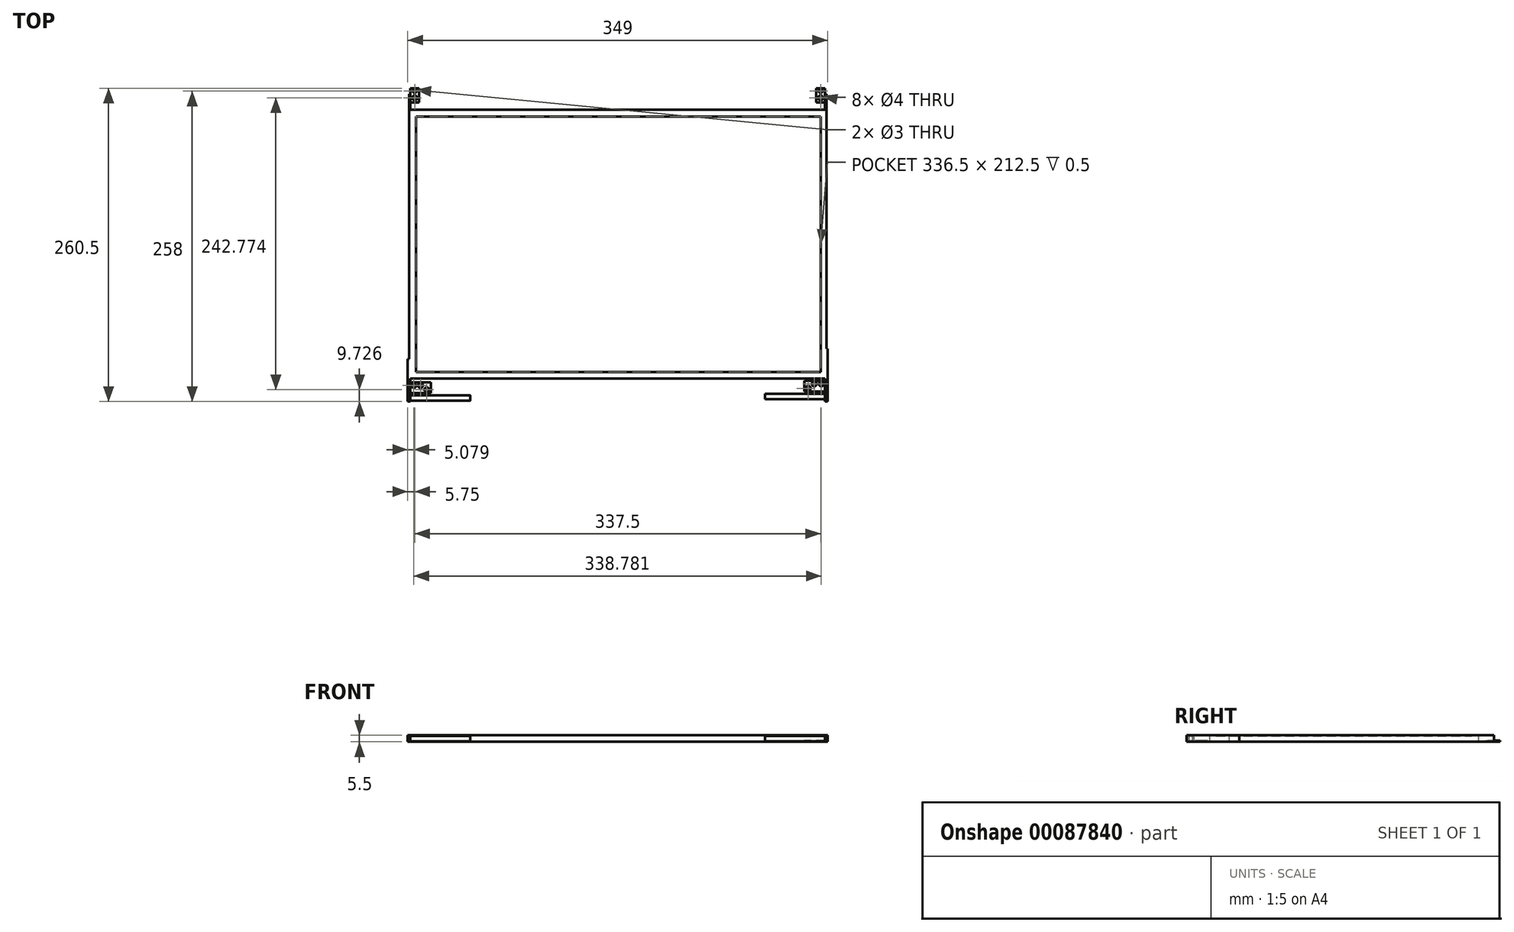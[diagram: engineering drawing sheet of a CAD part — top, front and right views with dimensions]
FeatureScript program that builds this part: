
annotation { "Feature Type Name" : "Feature", "Feature Type Description" : "" }
export const myFeature = defineFeature(function(context is Context, id is Id, definition is map)
    precondition{}
    {
        {
            var Q0;
            Q0=qCreatedBy(makeId("Top.planeOp"),FACE);
            var sketch = newSketch(context, id + "F0", { "sketchPlane" : qUnion([Q0])});
            skLineSegment(sketch, "E0.bottom", {"start": v(172.5, -111.75) * mm, "end": v(-172.5, -111.75) * mm});
            skLineSegment(sketch, "E0.top", {"start": v(172.5, 111.75) * mm, "end": v(-172.5, 111.75) * mm});
            skLineSegment(sketch, "E0.left", {"start": v(172.5, -111.75) * mm, "end": v(172.5, 111.75) * mm});
            skLineSegment(sketch, "E0.right", {"start": v(-172.5, -111.75) * mm, "end": v(-172.5, 111.75) * mm});
            skPoint(sketch, "E0.middle", {"position": v(0, 0) * mm});
            skSolve(sketch);
        }
        {
            var Q0;
            Q0 = qSketchRegion(id + "F0", true);
            extrude(context, id + "F1", {"entities" : qUnion([Q0]), "depth" : 5.5 * mm, "symmetric" : true});
        }
        {
            var Q0;
            Q0=makeQuery(id+"F1.opExtrude","CAP_FACE",FACE,{"disambiguationData":[OSD([sQuery(id+"F0.wireOp",EDGE,"E0.bottom"),sQuery(id+"F0.wireOp",EDGE,"E0.top"),sQuery(id+"F0.wireOp",EDGE,"E0.left"),sQuery(id+"F0.wireOp",EDGE,"E0.right")])],"isStart":false});
            var sketch = newSketch(context, id + "F2", { "sketchPlane" : qUnion([Q0])});
            skLineSegment(sketch, "E1.bottom", {"start": v(169, -106.25) * mm, "end": v(-167.5, -106.25) * mm});
            skLineSegment(sketch, "E1.top", {"start": v(169, 106.25) * mm, "end": v(-167.5, 106.25) * mm});
            skLineSegment(sketch, "E1.left", {"start": v(169, -106.25) * mm, "end": v(169, 106.25) * mm});
            skLineSegment(sketch, "E1.right", {"start": v(-167.5, -106.25) * mm, "end": v(-167.5, 106.25) * mm});
            skPoint(sketch, "E1.middle", {"position": v(0, 0) * mm});
            skSolve(sketch);
        }
        {
            var Q0;
            Q0 = qSketchRegion(id + "F2", true);
            var Q1;
            Q1 = qConstructionFilter(qBodyType(qCreatedBy(id + "F2" ,EDGE), BodyType.WIRE), ConstructionObject.NO);
            extrude(context, id + "F3", {"entities" : qUnion([Q0]), "operationType" : NewBodyOperationType.REMOVE, "surfaceEntities" : qUnion([Q1]), "oppositeDirection" : true, "depth" : 0.5 * mm});
        }
        {
            var Q0;
            Q0=makeQuery(id+"F1.opExtrude","SWEPT_FACE",FACE,{"disambiguationData":[OSD([sQuery(id+"F0.wireOp",EDGE,"E0.right")])]});
            var sketch = newSketch(context, id + "F4", { "sketchPlane" : qUnion([Q0])});
            skLineSegment(sketch, "E2", {"start": v(-124.75, 2.75) * mm, "end": v(-111.75, 2.75) * mm});
            skLineSegment(sketch, "E3", {"start": v(-111.75, 2.75) * mm, "end": v(111.75, 2.75) * mm});
            skLineSegment(sketch, "E4", {"start": v(111.75, 2.75) * mm, "end": v(130.75, 2.75) * mm});
            skLineSegment(sketch, "E5", {"start": v(130.75, 2.75) * mm, "end": v(130.75, -2.75) * mm});
            skLineSegment(sketch, "E6", {"start": v(130.75, -2.75) * mm, "end": v(111.75, -2.75) * mm});
            skLineSegment(sketch, "E7", {"start": v(111.75, -2.75) * mm, "end": v(-111.75, -2.75) * mm});
            skLineSegment(sketch, "E8", {"start": v(-111.75, -2.75) * mm, "end": v(-124.75, -2.75) * mm});
            skLineSegment(sketch, "E9", {"start": v(-124.75, -2.75) * mm, "end": v(-124.75, 2.75) * mm});
            skSolve(sketch);
        }
        {
            var Q0;
            Q0 = qSketchRegion(id + "F4", true);
            extrude(context, id + "F5", {"entities" : qUnion([Q0]), "operationType" : NewBodyOperationType.ADD, "depth" : 1 * mm});
        }
        {
            var Q0;
            Q0=makeQuery(id+"F1.opExtrude","SWEPT_FACE",FACE,{"disambiguationData":[OSD([sQuery(id+"F0.wireOp",EDGE,"E0.left")])]});
            var sketch = newSketch(context, id + "F6", { "sketchPlane" : qUnion([Q0])});
            skLineSegment(sketch, "E10", {"start": v(111.75, 2.75) * mm, "end": v(124.75, 2.75) * mm});
            skLineSegment(sketch, "E11", {"start": v(124.75, 2.75) * mm, "end": v(124.75, -2.75) * mm});
            skLineSegment(sketch, "E12", {"start": v(124.75, -2.75) * mm, "end": v(111.75, -2.75) * mm});
            skLineSegment(sketch, "E13", {"start": v(111.75, -2.75) * mm, "end": v(-111.75, -2.75) * mm});
            skLineSegment(sketch, "E14", {"start": v(-111.75, -2.75) * mm, "end": v(-130.75, -2.75) * mm});
            skLineSegment(sketch, "E15", {"start": v(-130.75, -2.75) * mm, "end": v(-130.75, 2.75) * mm});
            skLineSegment(sketch, "E16", {"start": v(-130.75, 2.75) * mm, "end": v(-111.75, 2.75) * mm});
            skLineSegment(sketch, "E17", {"start": v(-111.75, 2.75) * mm, "end": v(111.75, 2.75) * mm});
            skSolve(sketch);
        }
        {
            var Q0;
            Q0 = qSketchRegion(id + "F6", true);
            extrude(context, id + "F7", {"entities" : qUnion([Q0]), "operationType" : NewBodyOperationType.ADD, "depth" : 1 * mm});
        }
        {
            var Q0;
            Q0=makeQuery(id+"F7.boolean.opBoolean","MERGE",FACE,{"derivedFrom":[makeQuery(id+"F5.boolean.opBoolean","MERGE",FACE,{"derivedFrom":[makeQuery(id+"F1.opExtrude","CAP_FACE",FACE,{"disambiguationData":[OSD([sQuery(id+"F0.wireOp",EDGE,"E0.bottom"),sQuery(id+"F0.wireOp",EDGE,"E0.top"),sQuery(id+"F0.wireOp",EDGE,"E0.left"),sQuery(id+"F0.wireOp",EDGE,"E0.right")])],"isStart":true}),makeQuery(id+"F5.opExtrude","SWEPT_FACE",FACE,{"disambiguationData":[OSD([sQuery(id+"F4.wireOp",EDGE,"E6"),sQuery(id+"F4.wireOp",EDGE,"E7"),sQuery(id+"F4.wireOp",EDGE,"E8")])]})]}),makeQuery(id+"F7.opExtrude","SWEPT_FACE",FACE,{"disambiguationData":[OSD([sQuery(id+"F6.wireOp",EDGE,"E12"),sQuery(id+"F6.wireOp",EDGE,"E13"),sQuery(id+"F6.wireOp",EDGE,"E14")])]})]});
            var sketch = newSketch(context, id + "F8", { "sketchPlane" : qUnion([Q0])});
            skLineSegment(sketch, "E18", {"start": v(-172.5, -124.75) * mm, "end": v(-172.5, -117.75) * mm});
            skLineSegment(sketch, "E19", {"start": v(-172.5, -117.75) * mm, "end": v(-165, -117.75) * mm});
            skLineSegment(sketch, "E20", {"start": v(-165, -117.75) * mm, "end": v(-165, -129.75) * mm});
            skLineSegment(sketch, "E21", {"start": v(-165, -129.75) * mm, "end": v(-172.5, -129.75) * mm});
            skLineSegment(sketch, "E22", {"start": v(-172.5, -129.75) * mm, "end": v(-172.5, -124.75) * mm});
            skCircle(sketch, "E23", {"center": v(-168.75, -121.75) * mm, "radius": 2 * mm});
            skCircle(sketch, "E24", {"center": v(-168.75, -127.25) * mm, "radius": 1.5 * mm});
            skSolve(sketch);
        }
        {
            var Q0;
            Q0=makeQuery(id+"F8.imprint","IMPRINT",FACE,{"disambiguationData":[TD([[makeQuery(id+"F8.imprint","IMPRINT",EDGE,{"derivedFrom":sQuery(id+"F8.wireOp",EDGE,"E18")}),1.0]])]});
            extrude(context, id + "F9", {"entities" : qUnion([Q0]), "operationType" : NewBodyOperationType.ADD, "oppositeDirection" : true, "depth" : 1 * mm});
        }
        {
            var Q0;
            Q0=makeQuery(id+"F9.boolean.opBoolean","MERGE",FACE,{"derivedFrom":[makeQuery(id+"F7.boolean.opBoolean","MERGE",FACE,{"derivedFrom":[makeQuery(id+"F5.boolean.opBoolean","MERGE",FACE,{"derivedFrom":[makeQuery(id+"F1.opExtrude","CAP_FACE",FACE,{"disambiguationData":[OSD([sQuery(id+"F0.wireOp",EDGE,"E0.bottom"),sQuery(id+"F0.wireOp",EDGE,"E0.top"),sQuery(id+"F0.wireOp",EDGE,"E0.left"),sQuery(id+"F0.wireOp",EDGE,"E0.right")])],"isStart":true}),makeQuery(id+"F5.opExtrude","SWEPT_FACE",FACE,{"disambiguationData":[OSD([sQuery(id+"F4.wireOp",EDGE,"E6"),sQuery(id+"F4.wireOp",EDGE,"E7"),sQuery(id+"F4.wireOp",EDGE,"E8")])]})]}),makeQuery(id+"F7.opExtrude","SWEPT_FACE",FACE,{"disambiguationData":[OSD([sQuery(id+"F6.wireOp",EDGE,"E12"),sQuery(id+"F6.wireOp",EDGE,"E13"),sQuery(id+"F6.wireOp",EDGE,"E14")])]})]}),makeQuery(id+"F9.opExtrude","CAP_FACE",FACE,{"disambiguationData":[OSD([sQuery(id+"F8.wireOp",EDGE,"E18"),sQuery(id+"F8.wireOp",EDGE,"E19"),sQuery(id+"F8.wireOp",EDGE,"E20"),sQuery(id+"F8.wireOp",EDGE,"E21"),sQuery(id+"F8.wireOp",EDGE,"E22"),sQuery(id+"F8.wireOp",EDGE,"E23"),sQuery(id+"F8.wireOp",EDGE,"E24")])],"isStart":true})]});
            var sketch = newSketch(context, id + "F10", { "sketchPlane" : qUnion([Q0])});
            skLineSegment(sketch, "E25", {"start": v(165, -129.75) * mm, "end": v(165, -117.75) * mm});
            skLineSegment(sketch, "E26", {"start": v(165, -117.75) * mm, "end": v(172.5, -117.75) * mm});
            skLineSegment(sketch, "E27", {"start": v(172.5, -117.75) * mm, "end": v(172.5, -129.75) * mm});
            skLineSegment(sketch, "E28", {"start": v(172.5, -129.75) * mm, "end": v(165, -129.75) * mm});
            skCircle(sketch, "E29", {"center": v(168.75, -121.75) * mm, "radius": 2 * mm});
            skCircle(sketch, "E30", {"center": v(168.75, -127.25) * mm, "radius": 1.5 * mm});
            skPoint(sketch, "E31", {"position": v(172.5, -124.75) * mm});
            skSolve(sketch);
        }
        {
            var Q0;
            Q0=makeQuery(id+"F10.imprint","IMPRINT",FACE,{"disambiguationData":[TD([[makeQuery(id+"F10.imprint","IMPRINT",EDGE,{"derivedFrom":sQuery(id+"F10.wireOp",EDGE,"E25")}),-1.0]])]});
            extrude(context, id + "F11", {"entities" : qUnion([Q0]), "operationType" : NewBodyOperationType.ADD, "oppositeDirection" : true, "depth" : 1 * mm});
        }
        {
            var Q0;
            Q0=makeQuery(id+"F5.opExtrude","CAP_FACE",FACE,{"disambiguationData":[OSD([sQuery(id+"F4.wireOp",EDGE,"E2"),sQuery(id+"F4.wireOp",EDGE,"E3"),sQuery(id+"F4.wireOp",EDGE,"E4"),sQuery(id+"F4.wireOp",EDGE,"E5"),sQuery(id+"F4.wireOp",EDGE,"E6"),sQuery(id+"F4.wireOp",EDGE,"E7"),sQuery(id+"F4.wireOp",EDGE,"E8"),sQuery(id+"F4.wireOp",EDGE,"E9")])],"isStart":false});
            var sketch = newSketch(context, id + "F12", { "sketchPlane" : qUnion([Q0])});
            skLineSegment(sketch, "E32.bottom", {"start": v(130.75, 2.75) * mm, "end": v(95.48, 2.75) * mm});
            skLineSegment(sketch, "E32.top", {"start": v(130.75, -2.75) * mm, "end": v(95.48, -2.75) * mm});
            skLineSegment(sketch, "E32.left", {"start": v(130.75, 2.75) * mm, "end": v(130.75, -2.75) * mm});
            skLineSegment(sketch, "E32.right", {"start": v(95.48, 2.75) * mm, "end": v(95.48, -2.75) * mm});
            skSolve(sketch);
        }
        {
            var Q0;
            Q0=makeQuery(id+"F12.imprint","IMPRINT",FACE,{"disambiguationData":[TD([[makeQuery(id+"F12.imprint","IMPRINT",EDGE,{"derivedFrom":sQuery(id+"F12.wireOp",EDGE,"E32.bottom")}),-1.0]])]});
            extrude(context, id + "F13", {"entities" : qUnion([Q0]), "operationType" : NewBodyOperationType.ADD, "depth" : 1 * mm});
        }
        {
            var Q0;
            Q0=makeQuery(id+"F13.boolean.opBoolean","MERGE",FACE,{"derivedFrom":[makeQuery(id+"F11.boolean.opBoolean","MERGE",FACE,{"derivedFrom":[makeQuery(id+"F9.boolean.opBoolean","MERGE",FACE,{"derivedFrom":[makeQuery(id+"F7.boolean.opBoolean","MERGE",FACE,{"derivedFrom":[makeQuery(id+"F5.boolean.opBoolean","MERGE",FACE,{"derivedFrom":[makeQuery(id+"F1.opExtrude","CAP_FACE",FACE,{"disambiguationData":[OSD([sQuery(id+"F0.wireOp",EDGE,"E0.bottom"),sQuery(id+"F0.wireOp",EDGE,"E0.top"),sQuery(id+"F0.wireOp",EDGE,"E0.left"),sQuery(id+"F0.wireOp",EDGE,"E0.right")])],"isStart":true}),makeQuery(id+"F5.opExtrude","SWEPT_FACE",FACE,{"disambiguationData":[OSD([sQuery(id+"F4.wireOp",EDGE,"E6"),sQuery(id+"F4.wireOp",EDGE,"E7"),sQuery(id+"F4.wireOp",EDGE,"E8")])]})]}),makeQuery(id+"F7.opExtrude","SWEPT_FACE",FACE,{"disambiguationData":[OSD([sQuery(id+"F6.wireOp",EDGE,"E12"),sQuery(id+"F6.wireOp",EDGE,"E13"),sQuery(id+"F6.wireOp",EDGE,"E14")])]})]}),makeQuery(id+"F9.opExtrude","CAP_FACE",FACE,{"disambiguationData":[OSD([sQuery(id+"F8.wireOp",EDGE,"E18"),sQuery(id+"F8.wireOp",EDGE,"E19"),sQuery(id+"F8.wireOp",EDGE,"E20"),sQuery(id+"F8.wireOp",EDGE,"E21"),sQuery(id+"F8.wireOp",EDGE,"E22"),sQuery(id+"F8.wireOp",EDGE,"E23"),sQuery(id+"F8.wireOp",EDGE,"E24")])],"isStart":true})]}),makeQuery(id+"F11.opExtrude","CAP_FACE",FACE,{"disambiguationData":[OSD([sQuery(id+"F10.wireOp",EDGE,"E25"),sQuery(id+"F10.wireOp",EDGE,"E26"),sQuery(id+"F10.wireOp",EDGE,"E27"),sQuery(id+"F10.wireOp",EDGE,"E28"),sQuery(id+"F10.wireOp",EDGE,"E29"),sQuery(id+"F10.wireOp",EDGE,"E30")])],"isStart":true})]}),makeQuery(id+"F13.opExtrude","SWEPT_FACE",FACE,{"disambiguationData":[OSD([sQuery(id+"F12.wireOp",EDGE,"E32.top")])]})]});
            var sketch = newSketch(context, id + "F14", { "sketchPlane" : qUnion([Q0])});
            skLineSegment(sketch, "E33.bottom", {"start": v(-172.5, 123.78) * mm, "end": v(-155.28, 123.78) * mm});
            skLineSegment(sketch, "E33.top", {"start": v(-172.5, 114.86) * mm, "end": v(-155.28, 114.86) * mm});
            skLineSegment(sketch, "E33.left", {"start": v(-172.5, 123.78) * mm, "end": v(-172.5, 114.86) * mm});
            skLineSegment(sketch, "E33.right", {"start": v(-155.28, 123.78) * mm, "end": v(-155.28, 114.86) * mm});
            skCircle(sketch, "E34", {"center": v(-169.42, 117.54) * mm, "radius": 2 * mm});
            skCircle(sketch, "E35", {"center": v(-163.89, 117.54) * mm, "radius": 2 * mm});
            skCircle(sketch, "E36", {"center": v(-158.69, 121.02) * mm, "radius": 2 * mm});
            skSolve(sketch);
        }
        {
            var Q0;
            Q0=makeQuery(id+"F14.imprint","IMPRINT",FACE,{"disambiguationData":[TD([[makeQuery(id+"F14.imprint","IMPRINT",EDGE,{"derivedFrom":sQuery(id+"F14.wireOp",EDGE,"E33.bottom")}),-1.0]])]});
            extrude(context, id + "F15", {"entities" : qUnion([Q0]), "operationType" : NewBodyOperationType.ADD, "oppositeDirection" : true, "depth" : 1 * mm});
        }
        {
            var Q0;
            {var subQ0=sQuery(id+"F4.wireOp",EDGE,"E4");var subQ1=sQuery(id+"F4.wireOp",EDGE,"E3");var subQ2=sQuery(id+"F4.wireOp",EDGE,"E2");var subQ6=sQuery(id+"F0.wireOp",EDGE,"E0.bottom");var subQ7=sQuery(id+"F4.wireOp",EDGE,"E5");var subQ8=sQuery(id+"F4.wireOp",EDGE,"E8");var subQ9=sQuery(id+"F4.wireOp",EDGE,"E7");var subQ10=sQuery(id+"F4.wireOp",EDGE,"E6");Q0=makeQuery(id+"F5.boolean.opBoolean","SPLIT",FACE,{"disambiguationData":[TD([makeQuery(id+"F1.opExtrude","SWEPT_FACE",FACE,{"disambiguationData":[OSD([subQ6])]})])],"derivedFrom":makeQuery(id+"F5.opExtrude","CAP_FACE",FACE,{"disambiguationData":[OSD([subQ2,subQ1,subQ0,subQ7,subQ10,subQ9,subQ8,sQuery(id+"F4.wireOp",EDGE,"E9")])],"isStart":true})});}
            var sketch = newSketch(context, id + "F16", { "sketchPlane" : qUnion([Q0])});
            skCircle(sketch, "E37", {"center": v(-127.91, 0) * mm, "radius": 2.17 * mm});
            skSolve(sketch);
        }
        {
            var Q0;
            Q0 = qSketchRegion(id + "F16", true);
            extrude(context, id + "F17", {"entities" : qUnion([Q0]), "operationType" : NewBodyOperationType.ADD, "depth" : 50 * mm});
        }
        {
            var Q0;
            Q0=makeQuery(id+"F7.opExtrude","CAP_FACE",FACE,{"disambiguationData":[OSD([sQuery(id+"F6.wireOp",EDGE,"E10"),sQuery(id+"F6.wireOp",EDGE,"E11"),sQuery(id+"F6.wireOp",EDGE,"E12"),sQuery(id+"F6.wireOp",EDGE,"E13"),sQuery(id+"F6.wireOp",EDGE,"E14"),sQuery(id+"F6.wireOp",EDGE,"E15"),sQuery(id+"F6.wireOp",EDGE,"E16"),sQuery(id+"F6.wireOp",EDGE,"E17")])],"isStart":false});
            var sketch = newSketch(context, id + "F18", { "sketchPlane" : qUnion([Q0])});
            skLineSegment(sketch, "E38.bottom", {"start": v(-130.75, -2.75) * mm, "end": v(-86.94, -2.75) * mm});
            skLineSegment(sketch, "E38.top", {"start": v(-130.75, 2.75) * mm, "end": v(-86.94, 2.75) * mm});
            skLineSegment(sketch, "E38.left", {"start": v(-130.75, -2.75) * mm, "end": v(-130.75, 2.75) * mm});
            skLineSegment(sketch, "E38.right", {"start": v(-86.94, -2.75) * mm, "end": v(-86.94, 2.75) * mm});
            skSolve(sketch);
        }
        {
            var Q0;
            Q0=makeQuery(id+"F18.imprint","IMPRINT",FACE,{"disambiguationData":[TD([[makeQuery(id+"F18.imprint","IMPRINT",EDGE,{"derivedFrom":sQuery(id+"F18.wireOp",EDGE,"E38.bottom")}),-1.0]])]});
            extrude(context, id + "F19", {"entities" : qUnion([Q0]), "operationType" : NewBodyOperationType.ADD, "depth" : 1 * mm});
        }
        {
            var Q0;
            Q0=makeQuery(id+"F19.boolean.opBoolean","MERGE",FACE,{"derivedFrom":[makeQuery(id+"F15.boolean.opBoolean","MERGE",FACE,{"derivedFrom":[makeQuery(id+"F13.boolean.opBoolean","MERGE",FACE,{"derivedFrom":[makeQuery(id+"F11.boolean.opBoolean","MERGE",FACE,{"derivedFrom":[makeQuery(id+"F9.boolean.opBoolean","MERGE",FACE,{"derivedFrom":[makeQuery(id+"F7.boolean.opBoolean","MERGE",FACE,{"derivedFrom":[makeQuery(id+"F5.boolean.opBoolean","MERGE",FACE,{"derivedFrom":[makeQuery(id+"F1.opExtrude","CAP_FACE",FACE,{"disambiguationData":[OSD([sQuery(id+"F0.wireOp",EDGE,"E0.bottom"),sQuery(id+"F0.wireOp",EDGE,"E0.top"),sQuery(id+"F0.wireOp",EDGE,"E0.left"),sQuery(id+"F0.wireOp",EDGE,"E0.right")])],"isStart":true}),makeQuery(id+"F5.opExtrude","SWEPT_FACE",FACE,{"disambiguationData":[OSD([sQuery(id+"F4.wireOp",EDGE,"E6"),sQuery(id+"F4.wireOp",EDGE,"E7"),sQuery(id+"F4.wireOp",EDGE,"E8")])]})]}),makeQuery(id+"F7.opExtrude","SWEPT_FACE",FACE,{"disambiguationData":[OSD([sQuery(id+"F6.wireOp",EDGE,"E12"),sQuery(id+"F6.wireOp",EDGE,"E13"),sQuery(id+"F6.wireOp",EDGE,"E14")])]})]}),makeQuery(id+"F9.opExtrude","CAP_FACE",FACE,{"disambiguationData":[OSD([sQuery(id+"F8.wireOp",EDGE,"E18"),sQuery(id+"F8.wireOp",EDGE,"E19"),sQuery(id+"F8.wireOp",EDGE,"E20"),sQuery(id+"F8.wireOp",EDGE,"E21"),sQuery(id+"F8.wireOp",EDGE,"E22"),sQuery(id+"F8.wireOp",EDGE,"E23"),sQuery(id+"F8.wireOp",EDGE,"E24")])],"isStart":true})]}),makeQuery(id+"F11.opExtrude","CAP_FACE",FACE,{"disambiguationData":[OSD([sQuery(id+"F10.wireOp",EDGE,"E25"),sQuery(id+"F10.wireOp",EDGE,"E26"),sQuery(id+"F10.wireOp",EDGE,"E27"),sQuery(id+"F10.wireOp",EDGE,"E28"),sQuery(id+"F10.wireOp",EDGE,"E29"),sQuery(id+"F10.wireOp",EDGE,"E30")])],"isStart":true})]}),makeQuery(id+"F13.opExtrude","SWEPT_FACE",FACE,{"disambiguationData":[OSD([sQuery(id+"F12.wireOp",EDGE,"E32.top")])]})]}),makeQuery(id+"F15.opExtrude","CAP_FACE",FACE,{"disambiguationData":[OSD([sQuery(id+"F14.wireOp",EDGE,"E33.bottom"),sQuery(id+"F14.wireOp",EDGE,"E33.top"),sQuery(id+"F14.wireOp",EDGE,"E33.left"),sQuery(id+"F14.wireOp",EDGE,"E33.right"),sQuery(id+"F14.wireOp",EDGE,"E34"),sQuery(id+"F14.wireOp",EDGE,"E35"),sQuery(id+"F14.wireOp",EDGE,"E36")])],"isStart":true})]}),makeQuery(id+"F19.opExtrude","SWEPT_FACE",FACE,{"disambiguationData":[OSD([sQuery(id+"F18.wireOp",EDGE,"E38.bottom")])]})]});
            var sketch = newSketch(context, id + "F20", { "sketchPlane" : qUnion([Q0])});
            skLineSegment(sketch, "E39.bottom", {"start": v(172.5, 113.49) * mm, "end": v(155.17, 113.49) * mm});
            skLineSegment(sketch, "E39.top", {"start": v(172.5, 122.38) * mm, "end": v(155.17, 122.38) * mm});
            skLineSegment(sketch, "E39.left", {"start": v(172.5, 113.49) * mm, "end": v(172.5, 122.38) * mm});
            skLineSegment(sketch, "E39.right", {"start": v(155.17, 113.49) * mm, "end": v(155.17, 122.38) * mm});
            skCircle(sketch, "E40", {"center": v(169.36, 116.2) * mm, "radius": 2 * mm});
            skCircle(sketch, "E41", {"center": v(163.46, 116.2) * mm, "radius": 2 * mm});
            skCircle(sketch, "E42", {"center": v(158.49, 119.8) * mm, "radius": 2 * mm});
            skSolve(sketch);
        }
        {
            var Q0;
            Q0=makeQuery(id+"F20.imprint","IMPRINT",FACE,{"disambiguationData":[TD([[makeQuery(id+"F20.imprint","IMPRINT",EDGE,{"derivedFrom":sQuery(id+"F20.wireOp",EDGE,"E39.bottom")}),-1.0]])]});
            extrude(context, id + "F21", {"entities" : qUnion([Q0]), "operationType" : NewBodyOperationType.ADD, "oppositeDirection" : true, "depth" : 1 * mm});
        }
        {
            var Q0;
            {var subQ3=sQuery(id+"F0.wireOp",EDGE,"E0.bottom");var subQ4=sQuery(id+"F6.wireOp",EDGE,"E15");var subQ5=sQuery(id+"F6.wireOp",EDGE,"E17");var subQ6=sQuery(id+"F6.wireOp",EDGE,"E16");var subQ7=sQuery(id+"F6.wireOp",EDGE,"E10");var subQ8=sQuery(id+"F6.wireOp",EDGE,"E14");var subQ9=sQuery(id+"F6.wireOp",EDGE,"E13");var subQ10=sQuery(id+"F6.wireOp",EDGE,"E12");Q0=makeQuery(id+"F7.boolean.opBoolean","SPLIT",FACE,{"disambiguationData":[TD([makeQuery(id+"F1.opExtrude","SWEPT_FACE",FACE,{"disambiguationData":[OSD([subQ3])]})])],"derivedFrom":makeQuery(id+"F7.opExtrude","CAP_FACE",FACE,{"disambiguationData":[OSD([subQ7,sQuery(id+"F6.wireOp",EDGE,"E11"),subQ10,subQ9,subQ8,subQ4,subQ6,subQ5])],"isStart":true})});}
            var sketch = newSketch(context, id + "F22", { "sketchPlane" : qUnion([Q0])});
            skCircle(sketch, "E43", {"center": v(126.6, 0) * mm, "radius": 2.27 * mm});
            skSolve(sketch);
        }
        {
            var Q0;
            Q0=makeQuery(id+"F22.imprint","IMPRINT",FACE,{"disambiguationData":[TD([[makeQuery(id+"F22.imprint","IMPRINT",EDGE,{"derivedFrom":sQuery(id+"F22.wireOp",EDGE,"E43")}),1.0]])]});
            extrude(context, id + "F23", {"entities" : qUnion([Q0]), "operationType" : NewBodyOperationType.ADD, "depth" : 50 * mm});
        }
    });
